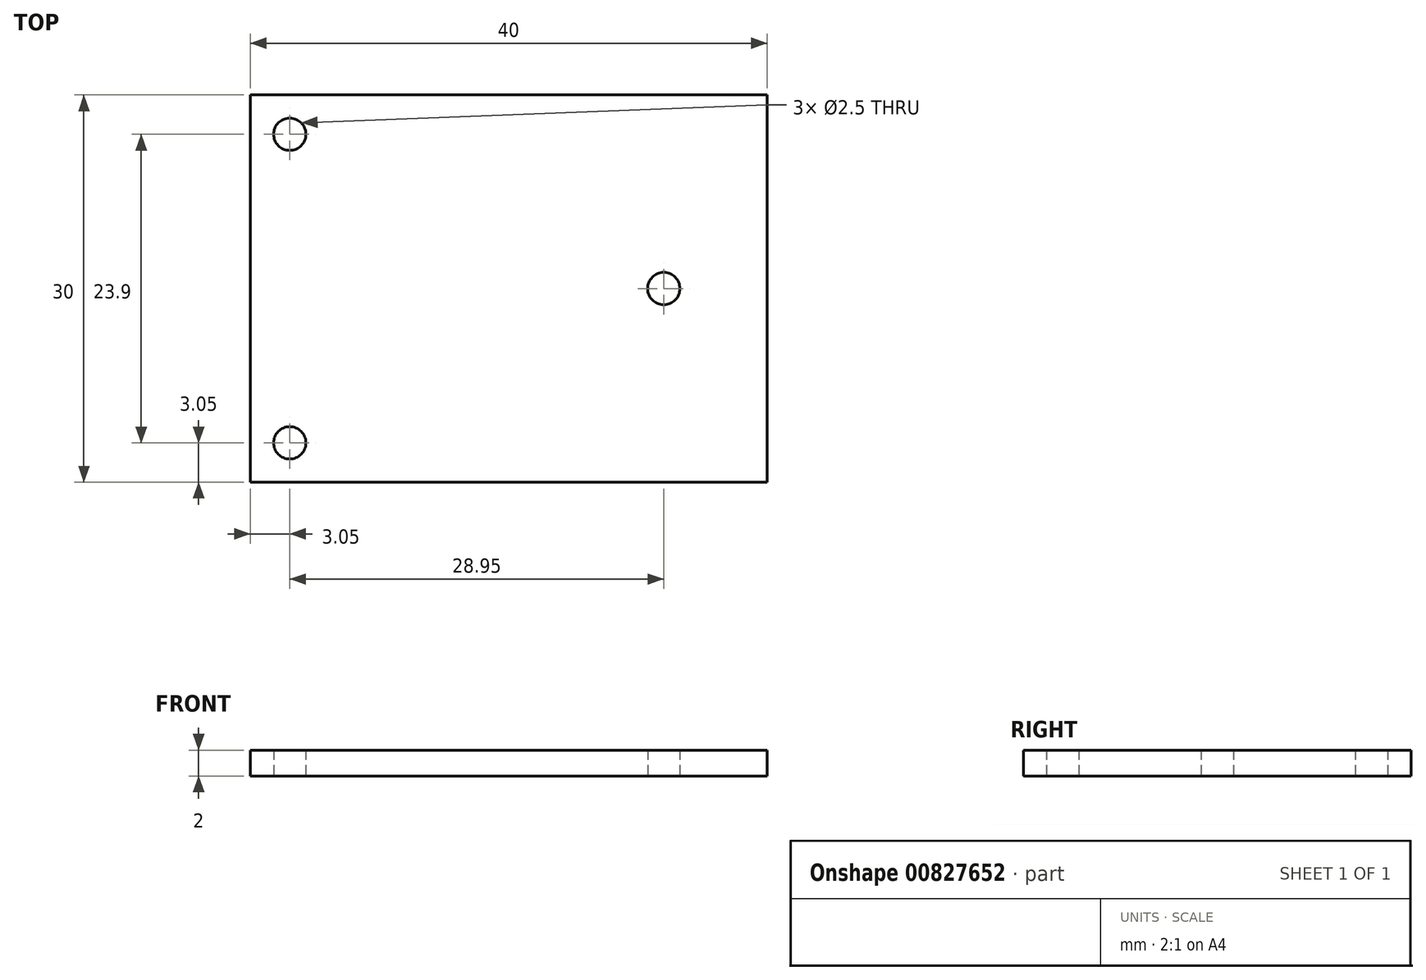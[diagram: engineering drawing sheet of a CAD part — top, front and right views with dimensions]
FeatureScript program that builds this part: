
annotation { "Feature Type Name" : "Feature", "Feature Type Description" : "" }
export const myFeature = defineFeature(function(context is Context, id is Id, definition is map)
    precondition{}
    {
        {
            var Q0;
            Q0=qCreatedBy(makeId("Top.planeOp"),FACE);
            var sketch = newSketch(context, id + "F0", { "sketchPlane" : qUnion([Q0])});
            skLineSegment(sketch, "E0.bottom", {"start": v(20, 15) * mm, "end": v(-20, 15) * mm});
            skLineSegment(sketch, "E0.top", {"start": v(20, -15) * mm, "end": v(-20, -15) * mm});
            skLineSegment(sketch, "E0.left", {"start": v(20, 15) * mm, "end": v(20, -15) * mm});
            skLineSegment(sketch, "E0.right", {"start": v(-20, 15) * mm, "end": v(-20, -15) * mm});
            skPoint(sketch, "E0.middle", {"position": v(0, 0) * mm});
            skCircle(sketch, "E1", {"center": v(-16.95, 11.95) * mm, "radius": 1.25 * mm});
            skCircle(sketch, "E2", {"center": v(-16.95, -11.95) * mm, "radius": 1.25 * mm});
            skCircle(sketch, "E3", {"center": v(12, 0) * mm, "radius": 1.25 * mm});
            skSolve(sketch);
        }
        {
            var Q0;
            Q0 = qSketchRegion(id + "F0", true);
            extrude(context, id + "F1", {"entities" : qUnion([Q0]), "depth" : 2 * mm, "offsetDistance" : 25.4 * mm});
        }
    });
